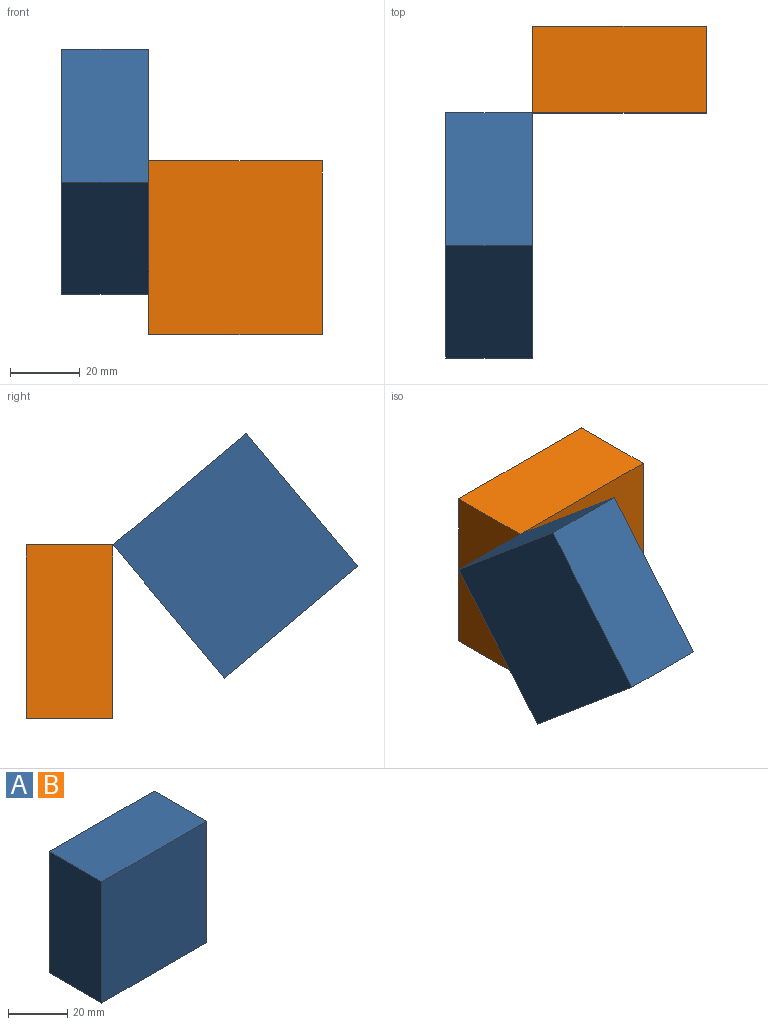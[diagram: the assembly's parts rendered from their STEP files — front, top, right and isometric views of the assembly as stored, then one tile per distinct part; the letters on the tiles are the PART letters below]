
ASSEMBLY  parts=2 mates=1
PART A: 6 faces, bbox 50x25x50 mm
  f0: plane 50x25mm, normal (0,0,1), area 1250mm2, adj f1,f3,f4,f5
  f1: plane 50x25mm, normal (-1,0,0), area 1250mm2, adj f0,f2,f4,f5
  f2: plane 50x25mm, normal (0,0,-1), area 1250mm2, adj f1,f3,f4,f5
  f3: plane 50x25mm, normal (1,0,0), area 1250mm2, adj f0,f2,f4,f5
  f4: plane 50x50mm, normal (0,-1,0), area 2500mm2, adj f0,f1,f2,f3
  f5: plane 50x50mm, normal (0,1,0), area 2500mm2, adj f0,f1,f2,f3
PART B: same geometry as A
PLACE A rot(axis=(-0.32,0.32,0.89),96.7deg) t=(72.99,-52.61,28.17)mm
PLACE B t=(118.95,-14.85,12.95)mm
MATE revolute A.f4 <-> B.f1  axis (1,0,0) through (97.99,-39.85,-1.81)mm
